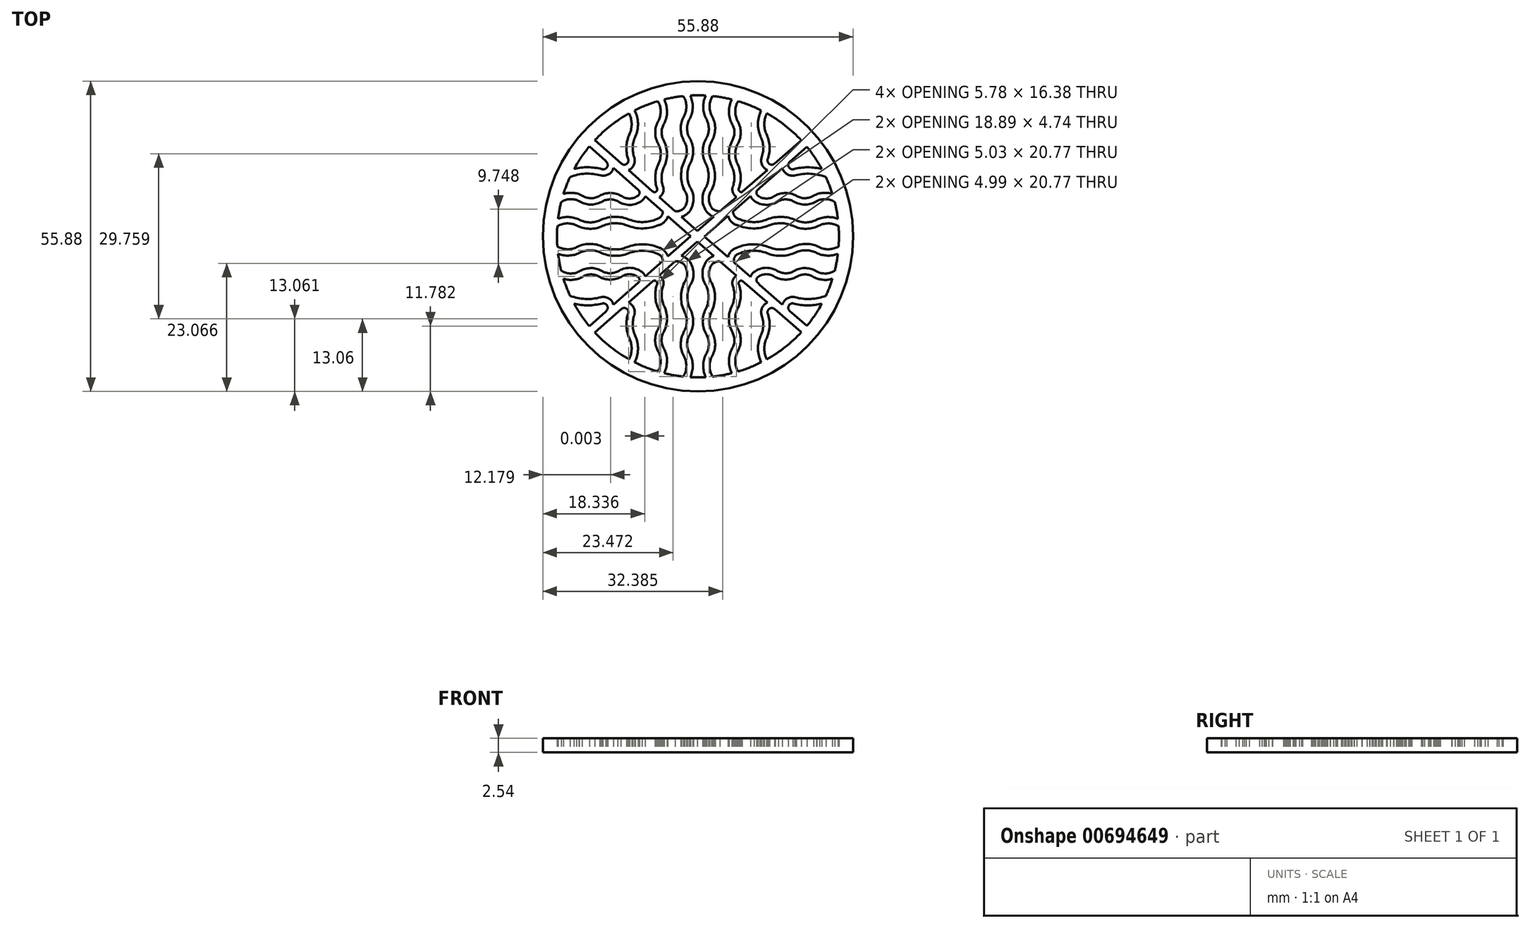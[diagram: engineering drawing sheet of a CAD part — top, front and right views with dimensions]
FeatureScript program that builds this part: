
annotation { "Feature Type Name" : "Feature", "Feature Type Description" : "" }
export const myFeature = defineFeature(function(context is Context, id is Id, definition is map)
    precondition{}
    {
        {
            var Q0;
            Q0=qCreatedBy(makeId("Top.planeOp"),FACE);
            var sketch = newSketch(context, id + "F0", { "sketchPlane" : qUnion([Q0])});
            skArc(sketch, "E0", {"start": v(11.4, 22.7) * mm, "mid": v(9.36, 23.61) * mm, "end": v(7.23, 24.35) * mm});
            skLineSegment(sketch, "E1.0", {"start": v(-19.59, 16.2) * mm, "end": v(-16.64, 13.58) * mm});
            skLineSegment(sketch, "E2.trimOffspring", {"start": v(-15.2, 12.3) * mm, "end": v(-11.27, 8.82) * mm});
            skLineSegment(sketch, "E3.trimOffspring", {"start": v(-9.5, 7.24) * mm, "end": v(-6.32, 4.43) * mm});
            skPoint(sketch, "E4.orphan", {"position": v(-12.42, 13.76) * mm});
            skLineSegment(sketch, "E5.trimOffspring", {"start": v(-12.5, 11.94) * mm, "end": v(-8.15, 8.09) * mm});
            skLineSegment(sketch, "E6.trimOffspring", {"start": v(-5.42, 3.63) * mm, "end": v(-1.33, 0) * mm});
            skPoint(sketch, "E7.endSnap0", {"position": v(-6.51, 7.74) * mm});
            skPoint(sketch, "E8.orphan", {"position": v(-7.23, 8.52) * mm});
            skLineSegment(sketch, "E9.trimOffspring", {"start": v(-6.99, 7.05) * mm, "end": v(-4.1, 4.5) * mm});
            skPoint(sketch, "E10.orphan", {"position": v(-2.63, 4.8) * mm});
            skLineSegment(sketch, "E11.trimOffspring", {"start": v(-2.98, 3.5) * mm, "end": v(-0.1, 0.94) * mm});
            skArc(sketch, "E12.MirrorCS", {"start": v(7.42, 3.1) * mm, "mid": v(6.64, 3.6) * mm, "end": v(6.32, 4.47) * mm});
            skLineSegment(sketch, "E13", {"start": v(19.61, 16.14) * mm, "end": v(16.53, 13.44) * mm});
            skPoint(sketch, "E14.orphan", {"position": v(5.96, 8.48) * mm});
            skLineSegment(sketch, "E15.trimOffspring", {"start": v(15.2, 12.28) * mm, "end": v(11.15, 8.71) * mm});
            skLineSegment(sketch, "E16.trimOffspring", {"start": v(12.5, 11.94) * mm, "end": v(8.02, 8.03) * mm});
            skPoint(sketch, "E17.orphan", {"position": v(12.33, 13.66) * mm});
            skLineSegment(sketch, "E18.trimOffspring", {"start": v(9.49, 7.26) * mm, "end": v(6.32, 4.47) * mm});
            skLineSegment(sketch, "E19.trimOffspring", {"start": v(6.94, 7.08) * mm, "end": v(3.98, 4.5) * mm});
            skLineSegment(sketch, "E20.trimOffspring", {"start": v(5.41, 3.68) * mm, "end": v(1.18, -0.03) * mm});
            skLineSegment(sketch, "E21.trimOffspring", {"start": v(2.87, 3.53) * mm, "end": v(-0.1, 0.94) * mm});
            skPoint(sketch, "E22.orphan", {"position": v(7.1, 8.47) * mm});
            skPoint(sketch, "E23.orphan", {"position": v(2.47, 4.78) * mm});
            skLineSegment(sketch, "E24", {"start": v(-1.33, 0) * mm, "end": v(-5.42, -3.63) * mm});
            skLineSegment(sketch, "E25", {"start": v(-0.1, -0.93) * mm, "end": v(-3, -3.49) * mm});
            skLineSegment(sketch, "E26.trimOffspring", {"start": v(-16.62, -13.56) * mm, "end": v(-19.58, -16.18) * mm});
            skLineSegment(sketch, "E27", {"start": v(-4.1, -4.5) * mm, "end": v(-6.99, -7.05) * mm});
            skLineSegment(sketch, "E28", {"start": v(-8.15, -8.09) * mm, "end": v(-12.5, -11.94) * mm});
            skLineSegment(sketch, "E29", {"start": v(-13.8, -13.1) * mm, "end": v(-18.57, -17.33) * mm});
            skPoint(sketch, "E30.MirrorP", {"position": v(12.33, -13.66) * mm});
            skLineSegment(sketch, "E31", {"start": v(-0.1, -0.93) * mm, "end": v(2.87, -3.53) * mm});
            skLineSegment(sketch, "E32", {"start": v(1.18, -0.03) * mm, "end": v(5.45, -3.76) * mm});
            skLineSegment(sketch, "E33", {"start": v(7.97, -7.99) * mm, "end": v(12.5, -11.94) * mm});
            skLineSegment(sketch, "E34", {"start": v(19.62, -16.13) * mm, "end": v(16.53, -13.44) * mm});
            skLineSegment(sketch, "E35.trimOffspring", {"start": v(3.98, -4.5) * mm, "end": v(6.94, -7.08) * mm});
            skLineSegment(sketch, "E36.trimOffspring", {"start": v(6.55, -4.72) * mm, "end": v(9.48, -7.28) * mm});
            skLineSegment(sketch, "E37.trimOffspring", {"start": v(15.2, -12.28) * mm, "end": v(11.14, -8.73) * mm});
            skPoint(sketch, "E38.orphan", {"position": v(-1.2, -0.1) * mm});
            skCircle(sketch, "E39.0", {"center": v(0, 0) * mm, "radius": 27.94 * mm});
            skArc(sketch, "E40.trimOffspring", {"start": v(6.1, 24.66) * mm, "mid": v(4.37, 25.02) * mm, "end": v(2.63, 25.26) * mm});
            skArc(sketch, "E41.trimOffspring", {"start": v(1.39, 25.36) * mm, "mid": v(0, 25.4) * mm, "end": v(-1.39, 25.36) * mm});
            skArc(sketch, "E42.trimOffspring", {"start": v(-2.63, 25.26) * mm, "mid": v(-4.37, 25.02) * mm, "end": v(-6.1, 24.66) * mm});
            skArc(sketch, "E43.trimOffspring", {"start": v(-7.23, 24.35) * mm, "mid": v(-9.36, 23.61) * mm, "end": v(-11.4, 22.7) * mm});
            skArc(sketch, "E44.trimOffspring", {"start": v(-12.42, 22.16) * mm, "mid": v(-15.68, 19.98) * mm, "end": v(-18.57, 17.33) * mm});
            skArc(sketch, "E45.trimOffspring", {"start": v(-19.58, 16.18) * mm, "mid": v(-21.04, 14.22) * mm, "end": v(-22.32, 12.13) * mm});
            skArc(sketch, "E46.trimOffspring", {"start": v(-23.03, 10.7) * mm, "mid": v(-23.68, 9.2) * mm, "end": v(-24.22, 7.64) * mm});
            skArc(sketch, "E47.trimOffspring", {"start": v(-24.63, 6.2) * mm, "mid": v(-24.96, 4.68) * mm, "end": v(-25.2, 3.15) * mm});
            skArc(sketch, "E48.trimOffspring", {"start": v(-25.33, 1.82) * mm, "mid": v(-25.4, 0) * mm, "end": v(-25.33, -1.82) * mm});
            skArc(sketch, "E49.trimOffspring", {"start": v(-25.2, -3.15) * mm, "mid": v(-24.96, -4.68) * mm, "end": v(-24.63, -6.2) * mm});
            skArc(sketch, "E50.trimOffspring", {"start": v(-22.32, -12.13) * mm, "mid": v(-21.04, -14.22) * mm, "end": v(-19.58, -16.18) * mm});
            skArc(sketch, "E51.trimOffspring", {"start": v(-18.57, -17.33) * mm, "mid": v(-15.68, -19.98) * mm, "end": v(-12.42, -22.16) * mm});
            skArc(sketch, "E52.trimOffspring", {"start": v(-11.4, -22.7) * mm, "mid": v(-9.36, -23.61) * mm, "end": v(-7.23, -24.35) * mm});
            skArc(sketch, "E53.trimOffspring", {"start": v(-6.1, -24.66) * mm, "mid": v(-4.37, -25.02) * mm, "end": v(-2.63, -25.26) * mm});
            skArc(sketch, "E54.trimOffspring", {"start": v(-1.39, -25.36) * mm, "mid": v(0, -25.4) * mm, "end": v(1.39, -25.36) * mm});
            skArc(sketch, "E55.trimOffspring", {"start": v(2.63, -25.26) * mm, "mid": v(4.37, -25.02) * mm, "end": v(6.1, -24.66) * mm});
            skArc(sketch, "E56.trimOffspring", {"start": v(7.23, -24.35) * mm, "mid": v(9.36, -23.61) * mm, "end": v(11.4, -22.7) * mm});
            skArc(sketch, "E57.trimOffspring", {"start": v(12.42, -22.16) * mm, "mid": v(15.7, -19.96) * mm, "end": v(18.62, -17.28) * mm});
            skArc(sketch, "E58.trimOffspring", {"start": v(19.62, -16.13) * mm, "mid": v(21.06, -14.2) * mm, "end": v(22.32, -12.13) * mm});
            skArc(sketch, "E59.trimOffspring", {"start": v(23.03, -10.7) * mm, "mid": v(23.68, -9.2) * mm, "end": v(24.22, -7.64) * mm});
            skArc(sketch, "E60.trimOffspring", {"start": v(24.63, -6.2) * mm, "mid": v(24.96, -4.68) * mm, "end": v(25.2, -3.15) * mm});
            skArc(sketch, "E61.trimOffspring", {"start": v(25.33, -1.82) * mm, "mid": v(25.4, 0) * mm, "end": v(25.33, 1.82) * mm});
            skArc(sketch, "E62.trimOffspring", {"start": v(25.2, 3.15) * mm, "mid": v(24.96, 4.68) * mm, "end": v(24.63, 6.2) * mm});
            skArc(sketch, "E63.trimOffspring", {"start": v(24.22, 7.64) * mm, "mid": v(23.68, 9.18) * mm, "end": v(23.05, 10.68) * mm});
            skArc(sketch, "E64.trimOffspring", {"start": v(22.33, 12.1) * mm, "mid": v(21.07, 14.19) * mm, "end": v(19.61, 16.14) * mm});
            skArc(sketch, "E65.trimOffspring", {"start": v(18.62, 17.28) * mm, "mid": v(15.7, 19.96) * mm, "end": v(12.42, 22.16) * mm});
            skArc(sketch, "E66", {"start": v(23.05, 10.68) * mm, "mid": v(20.32, 11.27) * mm, "end": v(17.54, 10.99) * mm});
            skArc(sketch, "E67.0", {"start": v(22.33, 12.1) * mm, "mid": v(19.79, 12.43) * mm, "end": v(17.25, 12.1) * mm});
            skArc(sketch, "E68", {"start": v(16.53, 13.44) * mm, "mid": v(16.36, 12.48) * mm, "end": v(17.25, 12.1) * mm});
            skArc(sketch, "E69.0", {"start": v(15.2, 12.28) * mm, "mid": v(16.11, 11.16) * mm, "end": v(17.54, 10.99) * mm});
            skArc(sketch, "E70.trimOffspring", {"start": v(15.67, 12.68) * mm, "mid": v(15.67, 12.68) * mm, "end": v(15.67, 12.69) * mm});
            skArc(sketch, "E71.MirrorCS", {"start": v(16.53, -13.44) * mm, "mid": v(16.36, -12.48) * mm, "end": v(17.24, -12.1) * mm});
            skArc(sketch, "E72.MirrorCS", {"start": v(15.2, -12.28) * mm, "mid": v(16.11, -11.17) * mm, "end": v(17.53, -10.99) * mm});
            skArc(sketch, "E73.MirrorCS", {"start": v(22.32, -12.13) * mm, "mid": v(19.78, -12.44) * mm, "end": v(17.24, -12.1) * mm});
            skArc(sketch, "E74.MirrorCS", {"start": v(23.03, -10.7) * mm, "mid": v(20.3, -11.28) * mm, "end": v(17.53, -10.99) * mm});
            skPoint(sketch, "E75.orphan", {"position": v(15.2, -12.28) * mm});
            skPoint(sketch, "E76.endSnap0", {"position": v(0, -25.4) * mm});
            skArc(sketch, "E77.MirrorCS", {"start": v(-16.53, -13.44) * mm, "mid": v(-16.36, -12.48) * mm, "end": v(-17.24, -12.1) * mm});
            skArc(sketch, "E78.MirrorCS", {"start": v(-15.2, -12.3) * mm, "mid": v(-16.1, -11.17) * mm, "end": v(-17.53, -10.99) * mm});
            skArc(sketch, "E79.MirrorCS", {"start": v(-23.03, -10.7) * mm, "mid": v(-20.3, -11.28) * mm, "end": v(-17.53, -10.99) * mm});
            skArc(sketch, "E80.MirrorCS", {"start": v(-22.32, -12.13) * mm, "mid": v(-19.78, -12.44) * mm, "end": v(-17.24, -12.1) * mm});
            skArc(sketch, "E81.MirrorCS", {"start": v(-16.53, 13.44) * mm, "mid": v(-16.36, 12.48) * mm, "end": v(-17.24, 12.1) * mm});
            skArc(sketch, "E82.MirrorCS", {"start": v(-22.32, 12.13) * mm, "mid": v(-19.78, 12.44) * mm, "end": v(-17.24, 12.1) * mm});
            skArc(sketch, "E83.MirrorCS", {"start": v(-23.03, 10.7) * mm, "mid": v(-20.3, 11.28) * mm, "end": v(-17.53, 10.99) * mm});
            skArc(sketch, "E84.MirrorCS", {"start": v(-15.2, 12.3) * mm, "mid": v(-16.1, 11.17) * mm, "end": v(-17.53, 10.99) * mm});
            skPoint(sketch, "E85.orphan", {"position": v(-15.2, 12.28) * mm});
            skLineSegment(sketch, "E86", {"start": v(-16.64, 13.58) * mm, "end": v(-16.53, 13.44) * mm});
            skPoint(sketch, "E87.orphan", {"position": v(-15.2, -12.28) * mm});
            skLineSegment(sketch, "E88", {"start": v(-16.62, -13.56) * mm, "end": v(-16.53, -13.44) * mm});
            skArc(sketch, "E89", {"start": v(-12.42, -22.16) * mm, "mid": v(-11.95, -20.32) * mm, "end": v(-12.31, -18.46) * mm});
            skArc(sketch, "E90.0", {"start": v(-11.4, -22.7) * mm, "mid": v(-10.81, -20.35) * mm, "end": v(-11.27, -17.98) * mm});
            skArc(sketch, "E91", {"start": v(-11.44, -14.13) * mm, "mid": v(-11.76, -16.08) * mm, "end": v(-11.27, -17.98) * mm});
            skArc(sketch, "E92.0", {"start": v(-12.55, -13.83) * mm, "mid": v(-12.9, -16.17) * mm, "end": v(-12.31, -18.46) * mm});
            skArc(sketch, "E93", {"start": v(-12.55, -13.83) * mm, "mid": v(-12.9, -13.01) * mm, "end": v(-13.8, -13.1) * mm});
            skArc(sketch, "E94.0", {"start": v(-11.42, -14.03) * mm, "mid": v(-11.6, -12.8) * mm, "end": v(-12.5, -11.94) * mm});
            skLineSegment(sketch, "E95", {"start": v(-11.42, -14.03) * mm, "end": v(-11.44, -14.13) * mm});
            skArc(sketch, "E96.MirrorCS", {"start": v(12.55, -13.83) * mm, "mid": v(12.9, -13.01) * mm, "end": v(13.8, -13.1) * mm});
            skArc(sketch, "E97.MirrorCS", {"start": v(11.42, -14.03) * mm, "mid": v(11.6, -12.8) * mm, "end": v(12.5, -11.94) * mm});
            skArc(sketch, "E98.MirrorCS", {"start": v(11.44, -14.13) * mm, "mid": v(11.76, -16.08) * mm, "end": v(11.27, -17.98) * mm});
            skArc(sketch, "E99.MirrorCS", {"start": v(12.55, -13.83) * mm, "mid": v(12.9, -16.17) * mm, "end": v(12.31, -18.46) * mm});
            skLineSegment(sketch, "E100.MirrorCS", {"start": v(11.42, -14.03) * mm, "end": v(11.44, -14.13) * mm});
            skArc(sketch, "E101.MirrorCS", {"start": v(12.42, -22.16) * mm, "mid": v(11.95, -20.32) * mm, "end": v(12.31, -18.46) * mm});
            skArc(sketch, "E102.MirrorCS", {"start": v(11.4, -22.7) * mm, "mid": v(10.81, -20.35) * mm, "end": v(11.27, -17.98) * mm});
            skLineSegment(sketch, "E103", {"start": v(18.62, -17.28) * mm, "end": v(13.8, -13.1) * mm});
            skPoint(sketch, "E104.orphan", {"position": v(12.5, -11.94) * mm});
            skArc(sketch, "E105.MirrorCS", {"start": v(12.55, 13.83) * mm, "mid": v(12.9, 16.17) * mm, "end": v(12.31, 18.46) * mm});
            skArc(sketch, "E106.MirrorCS", {"start": v(11.44, 14.13) * mm, "mid": v(11.76, 16.08) * mm, "end": v(11.27, 17.98) * mm});
            skArc(sketch, "E107.MirrorCS", {"start": v(11.4, 22.7) * mm, "mid": v(10.81, 20.35) * mm, "end": v(11.27, 17.98) * mm});
            skArc(sketch, "E108.MirrorCS", {"start": v(12.42, 22.16) * mm, "mid": v(11.95, 20.32) * mm, "end": v(12.31, 18.46) * mm});
            skArc(sketch, "E109.MirrorCS", {"start": v(11.42, 14.03) * mm, "mid": v(11.6, 12.8) * mm, "end": v(12.5, 11.94) * mm});
            skArc(sketch, "E110.MirrorCS", {"start": v(12.55, 13.83) * mm, "mid": v(12.9, 13.01) * mm, "end": v(13.8, 13.1) * mm});
            skLineSegment(sketch, "E111.MirrorCS", {"start": v(11.42, 14.03) * mm, "end": v(11.44, 14.13) * mm});
            skLineSegment(sketch, "E112", {"start": v(13.8, 13.1) * mm, "end": v(18.62, 17.28) * mm});
            skArc(sketch, "E113.MirrorCS", {"start": v(-11.4, 22.7) * mm, "mid": v(-10.81, 20.35) * mm, "end": v(-11.27, 17.98) * mm});
            skArc(sketch, "E114.MirrorCS", {"start": v(-12.42, 22.16) * mm, "mid": v(-11.95, 20.32) * mm, "end": v(-12.31, 18.46) * mm});
            skArc(sketch, "E115.MirrorCS", {"start": v(-12.55, 13.84) * mm, "mid": v(-12.9, 16.17) * mm, "end": v(-12.31, 18.46) * mm});
            skArc(sketch, "E116.MirrorCS", {"start": v(-11.44, 14.13) * mm, "mid": v(-11.76, 16.08) * mm, "end": v(-11.27, 17.98) * mm});
            skLineSegment(sketch, "E117.MirrorCS", {"start": v(-11.42, 14.03) * mm, "end": v(-11.44, 14.13) * mm});
            skArc(sketch, "E118.MirrorCS", {"start": v(-11.42, 14.03) * mm, "mid": v(-11.6, 12.8) * mm, "end": v(-12.5, 11.94) * mm});
            skArc(sketch, "E119.MirrorCS", {"start": v(-12.55, 13.84) * mm, "mid": v(-12.9, 13.01) * mm, "end": v(-13.8, 13.1) * mm});
            skPoint(sketch, "E120.orphan", {"position": v(-12.5, 11.94) * mm});
            skLineSegment(sketch, "E121", {"start": v(-18.57, 17.33) * mm, "end": v(-13.8, 13.1) * mm});
            skArc(sketch, "E122", {"start": v(-24.63, -6.2) * mm, "mid": v(-23.05, -6.7) * mm, "end": v(-21.43, -6.35) * mm});
            skArc(sketch, "E123.0", {"start": v(-24.22, -7.64) * mm, "mid": v(-22.5, -7.83) * mm, "end": v(-20.86, -7.34) * mm});
            skArc(sketch, "E124", {"start": v(-17.73, -7.31) * mm, "mid": v(-19.3, -6.87) * mm, "end": v(-20.86, -7.34) * mm});
            skArc(sketch, "E125.0", {"start": v(-17.39, -6.2) * mm, "mid": v(-19.43, -5.73) * mm, "end": v(-21.43, -6.35) * mm});
            skArc(sketch, "E126", {"start": v(-17.39, -6.2) * mm, "mid": v(-15.96, -6.65) * mm, "end": v(-14.49, -6.36) * mm});
            skArc(sketch, "E127.0", {"start": v(-17.73, -7.31) * mm, "mid": v(-15.81, -7.8) * mm, "end": v(-13.9, -7.34) * mm});
            skArc(sketch, "E128", {"start": v(-10.78, -7.34) * mm, "mid": v(-12.34, -6.82) * mm, "end": v(-13.9, -7.34) * mm});
            skArc(sketch, "E129.0", {"start": v(-10.1, -6.42) * mm, "mid": v(-12.28, -5.67) * mm, "end": v(-14.49, -6.36) * mm});
            skArc(sketch, "E130", {"start": v(-10.78, -8.38) * mm, "mid": v(-10.53, -7.86) * mm, "end": v(-10.78, -7.34) * mm});
            skArc(sketch, "E131.0", {"start": v(-9.5, -7.24) * mm, "mid": v(-9.73, -6.8) * mm, "end": v(-10.08, -6.43) * mm});
            skLineSegment(sketch, "E132.trimOffspring", {"start": v(-10.74, -8.34) * mm, "end": v(-15.2, -12.3) * mm});
            skLineSegment(sketch, "E133", {"start": v(-10.1, -6.42) * mm, "end": v(-10.08, -6.43) * mm});
            skArc(sketch, "E134.MirrorCS", {"start": v(24.22, -7.64) * mm, "mid": v(22.5, -7.83) * mm, "end": v(20.86, -7.34) * mm});
            skArc(sketch, "E135.MirrorCS", {"start": v(24.63, -6.2) * mm, "mid": v(23.05, -6.7) * mm, "end": v(21.43, -6.35) * mm});
            skArc(sketch, "E136.MirrorCS", {"start": v(17.39, -6.2) * mm, "mid": v(19.43, -5.73) * mm, "end": v(21.43, -6.35) * mm});
            skArc(sketch, "E137.MirrorCS", {"start": v(17.73, -7.31) * mm, "mid": v(19.3, -6.87) * mm, "end": v(20.86, -7.34) * mm});
            skArc(sketch, "E138.MirrorCS", {"start": v(17.39, -6.2) * mm, "mid": v(15.96, -6.65) * mm, "end": v(14.49, -6.36) * mm});
            skArc(sketch, "E139.MirrorCS", {"start": v(17.73, -7.31) * mm, "mid": v(15.81, -7.8) * mm, "end": v(13.9, -7.34) * mm});
            skArc(sketch, "E140.MirrorCS", {"start": v(10.1, -6.42) * mm, "mid": v(12.28, -5.67) * mm, "end": v(14.49, -6.36) * mm});
            skArc(sketch, "E141.MirrorCS", {"start": v(10.78, -7.34) * mm, "mid": v(12.34, -6.82) * mm, "end": v(13.9, -7.34) * mm});
            skArc(sketch, "E142.MirrorCS", {"start": v(10.78, -8.38) * mm, "mid": v(10.53, -7.86) * mm, "end": v(10.78, -7.34) * mm});
            skArc(sketch, "E143.MirrorCS", {"start": v(9.48, -7.28) * mm, "mid": v(9.72, -6.81) * mm, "end": v(10.08, -6.43) * mm});
            skLineSegment(sketch, "E144.MirrorCS", {"start": v(10.1, -6.42) * mm, "end": v(10.08, -6.43) * mm});
            skPoint(sketch, "E145.orphan", {"position": v(9.5, -7.24) * mm});
            skLineSegment(sketch, "E146", {"start": v(11.14, -8.73) * mm, "end": v(10.78, -8.38) * mm});
            skArc(sketch, "E147.MirrorCS", {"start": v(10.1, 6.42) * mm, "mid": v(12.28, 5.67) * mm, "end": v(14.49, 6.36) * mm});
            skArc(sketch, "E148.MirrorCS", {"start": v(9.49, 7.26) * mm, "mid": v(9.72, 6.8) * mm, "end": v(10.08, 6.43) * mm});
            skArc(sketch, "E149.MirrorCS", {"start": v(10.78, 7.34) * mm, "mid": v(12.34, 6.82) * mm, "end": v(13.9, 7.34) * mm});
            skArc(sketch, "E150.MirrorCS", {"start": v(10.78, 8.38) * mm, "mid": v(10.53, 7.86) * mm, "end": v(10.78, 7.34) * mm});
            skArc(sketch, "E151.MirrorCS", {"start": v(17.73, 7.31) * mm, "mid": v(15.81, 7.8) * mm, "end": v(13.9, 7.34) * mm});
            skArc(sketch, "E152.MirrorCS", {"start": v(17.39, 6.2) * mm, "mid": v(15.96, 6.65) * mm, "end": v(14.49, 6.36) * mm});
            skArc(sketch, "E153.MirrorCS", {"start": v(17.73, 7.31) * mm, "mid": v(19.3, 6.87) * mm, "end": v(20.86, 7.34) * mm});
            skArc(sketch, "E154.MirrorCS", {"start": v(17.39, 6.2) * mm, "mid": v(19.43, 5.73) * mm, "end": v(21.43, 6.35) * mm});
            skArc(sketch, "E155.MirrorCS", {"start": v(24.22, 7.64) * mm, "mid": v(22.5, 7.83) * mm, "end": v(20.86, 7.34) * mm});
            skArc(sketch, "E156.MirrorCS", {"start": v(24.63, 6.2) * mm, "mid": v(23.05, 6.7) * mm, "end": v(21.43, 6.35) * mm});
            skLineSegment(sketch, "E157", {"start": v(11.15, 8.71) * mm, "end": v(10.78, 8.38) * mm});
            skPoint(sketch, "E158.orphan", {"position": v(9.48, 7.28) * mm});
            skLineSegment(sketch, "E159", {"start": v(10.08, 6.43) * mm, "end": v(10.1, 6.42) * mm});
            skArc(sketch, "E160.MirrorCS", {"start": v(-10.78, 8.38) * mm, "mid": v(-10.53, 7.86) * mm, "end": v(-10.78, 7.34) * mm});
            skArc(sketch, "E161.MirrorCS", {"start": v(-9.5, 7.24) * mm, "mid": v(-9.74, 6.78) * mm, "end": v(-10.11, 6.4) * mm});
            skArc(sketch, "E162.MirrorCS", {"start": v(-10.11, 6.4) * mm, "mid": v(-12.3, 5.67) * mm, "end": v(-14.49, 6.36) * mm});
            skArc(sketch, "E163.MirrorCS", {"start": v(-10.78, 7.34) * mm, "mid": v(-12.34, 6.82) * mm, "end": v(-13.9, 7.34) * mm});
            skArc(sketch, "E164.MirrorCS", {"start": v(-17.38, 6.2) * mm, "mid": v(-15.95, 6.65) * mm, "end": v(-14.49, 6.36) * mm});
            skArc(sketch, "E165.MirrorCS", {"start": v(-17.73, 7.31) * mm, "mid": v(-15.81, 7.8) * mm, "end": v(-13.9, 7.34) * mm});
            skArc(sketch, "E166.MirrorCS", {"start": v(-17.17, 6.32) * mm, "mid": v(-19.3, 5.72) * mm, "end": v(-21.43, 6.35) * mm});
            skArc(sketch, "E167.MirrorCS", {"start": v(-17.73, 7.31) * mm, "mid": v(-19.3, 6.87) * mm, "end": v(-20.86, 7.34) * mm});
            skArc(sketch, "E168.MirrorCS", {"start": v(-24.63, 6.2) * mm, "mid": v(-23.05, 6.7) * mm, "end": v(-21.43, 6.35) * mm});
            skArc(sketch, "E169.MirrorCS", {"start": v(-24.22, 7.64) * mm, "mid": v(-22.5, 7.83) * mm, "end": v(-20.86, 7.34) * mm});
            skLineSegment(sketch, "E170", {"start": v(-11.27, 8.82) * mm, "end": v(-10.78, 8.38) * mm});
            skPoint(sketch, "E171.orphan", {"position": v(-10.4, 8.04) * mm});
            skArc(sketch, "E172", {"start": v(-7.09, 20.86) * mm, "mid": v(-6.72, 22.62) * mm, "end": v(-7.23, 24.35) * mm});
            skArc(sketch, "E173.0", {"start": v(-6.09, 20.3) * mm, "mid": v(-5.57, 22.48) * mm, "end": v(-6.1, 24.66) * mm});
            skArc(sketch, "E174", {"start": v(-6.09, 20.3) * mm, "mid": v(-6.56, 18.84) * mm, "end": v(-6.22, 17.34) * mm});
            skArc(sketch, "E175.0", {"start": v(-7.09, 20.86) * mm, "mid": v(-7.7, 18.85) * mm, "end": v(-7.22, 16.8) * mm});
            skArc(sketch, "E176", {"start": v(-7.12, 13.06) * mm, "mid": v(-6.7, 14.94) * mm, "end": v(-7.22, 16.8) * mm});
            skArc(sketch, "E177.0", {"start": v(-6.1, 12.56) * mm, "mid": v(-5.57, 14.97) * mm, "end": v(-6.22, 17.34) * mm});
            skArc(sketch, "E178", {"start": v(-6.1, 12.56) * mm, "mid": v(-6.56, 10.74) * mm, "end": v(-6.25, 8.88) * mm});
            skArc(sketch, "E179.0", {"start": v(-7.12, 13.06) * mm, "mid": v(-7.7, 10.83) * mm, "end": v(-7.34, 8.54) * mm});
            skArc(sketch, "E180", {"start": v(-8.15, 8.09) * mm, "mid": v(-7.58, 8.03) * mm, "end": v(-7.34, 8.54) * mm});
            skArc(sketch, "E181.0", {"start": v(-6.99, 7.05) * mm, "mid": v(-6.31, 7.84) * mm, "end": v(-6.25, 8.88) * mm});
            skArc(sketch, "E182.MirrorCS", {"start": v(-6.99, -7.05) * mm, "mid": v(-6.31, -7.84) * mm, "end": v(-6.25, -8.88) * mm});
            skArc(sketch, "E183.MirrorCS", {"start": v(-8.15, -8.09) * mm, "mid": v(-7.58, -8.03) * mm, "end": v(-7.34, -8.54) * mm});
            skArc(sketch, "E184.MirrorCS", {"start": v(-7.12, -13.07) * mm, "mid": v(-7.7, -10.83) * mm, "end": v(-7.34, -8.54) * mm});
            skArc(sketch, "E185.MirrorCS", {"start": v(-6.09, -12.56) * mm, "mid": v(-6.56, -10.74) * mm, "end": v(-6.25, -8.88) * mm});
            skArc(sketch, "E186.MirrorCS", {"start": v(-7.12, -13.07) * mm, "mid": v(-6.72, -14.94) * mm, "end": v(-7.23, -16.8) * mm});
            skArc(sketch, "E187.MirrorCS", {"start": v(-6.09, -12.56) * mm, "mid": v(-5.57, -14.97) * mm, "end": v(-6.23, -17.34) * mm});
            skArc(sketch, "E188.MirrorCS", {"start": v(-7.09, -20.86) * mm, "mid": v(-7.7, -18.85) * mm, "end": v(-7.23, -16.8) * mm});
            skArc(sketch, "E189.MirrorCS", {"start": v(-6.09, -20.3) * mm, "mid": v(-6.56, -18.84) * mm, "end": v(-6.23, -17.34) * mm});
            skArc(sketch, "E190.MirrorCS", {"start": v(-7.09, -20.86) * mm, "mid": v(-6.72, -22.62) * mm, "end": v(-7.23, -24.35) * mm});
            skArc(sketch, "E191.MirrorCS", {"start": v(-6.09, -20.3) * mm, "mid": v(-5.57, -22.48) * mm, "end": v(-6.1, -24.66) * mm});
            skArc(sketch, "E192.MirrorCS", {"start": v(-6.09, -20.3) * mm, "mid": v(-5.57, -22.47) * mm, "end": v(-6.09, -24.64) * mm});
            skPoint(sketch, "E193.orphan", {"position": v(-6.09, -24.64) * mm});
            skArc(sketch, "E194.MirrorCS", {"start": v(6.94, -7.08) * mm, "mid": v(6.26, -8) * mm, "end": v(6.34, -9.13) * mm});
            skArc(sketch, "E195.MirrorCS", {"start": v(7.97, -7.99) * mm, "mid": v(7.5, -8.09) * mm, "end": v(7.34, -8.54) * mm});
            skArc(sketch, "E196.MirrorCS", {"start": v(7.12, -13.07) * mm, "mid": v(7.7, -10.83) * mm, "end": v(7.34, -8.54) * mm});
            skArc(sketch, "E197.MirrorCS", {"start": v(6.09, -12.57) * mm, "mid": v(6.55, -10.87) * mm, "end": v(6.34, -9.13) * mm});
            skArc(sketch, "E198.MirrorCS", {"start": v(7.12, -13.07) * mm, "mid": v(6.72, -14.94) * mm, "end": v(7.23, -16.8) * mm});
            skArc(sketch, "E199.MirrorCS", {"start": v(6.09, -12.57) * mm, "mid": v(5.57, -14.97) * mm, "end": v(6.23, -17.34) * mm});
            skArc(sketch, "E200.MirrorCS", {"start": v(7.09, -20.86) * mm, "mid": v(7.7, -18.85) * mm, "end": v(7.23, -16.8) * mm});
            skArc(sketch, "E201.MirrorCS", {"start": v(6.09, -20.3) * mm, "mid": v(6.56, -18.84) * mm, "end": v(6.23, -17.34) * mm});
            skArc(sketch, "E202.MirrorCS", {"start": v(6.09, -20.3) * mm, "mid": v(5.57, -22.48) * mm, "end": v(6.1, -24.66) * mm});
            skArc(sketch, "E203.MirrorCS", {"start": v(7.09, -20.86) * mm, "mid": v(6.72, -22.62) * mm, "end": v(7.23, -24.35) * mm});
            skPoint(sketch, "E204.orphan", {"position": v(6.99, -7.05) * mm});
            skPoint(sketch, "E205.orphan", {"position": v(8.15, -8.09) * mm});
            skArc(sketch, "E206.MirrorCS", {"start": v(7.97, 7.99) * mm, "mid": v(7.5, 8.09) * mm, "end": v(7.34, 8.54) * mm});
            skArc(sketch, "E207.MirrorCS", {"start": v(6.94, 7.08) * mm, "mid": v(6.3, 7.87) * mm, "end": v(6.25, 8.88) * mm});
            skArc(sketch, "E208.MirrorCS", {"start": v(7.12, 13.07) * mm, "mid": v(7.7, 10.83) * mm, "end": v(7.34, 8.54) * mm});
            skArc(sketch, "E209.MirrorCS", {"start": v(6.09, 12.57) * mm, "mid": v(6.56, 10.74) * mm, "end": v(6.25, 8.88) * mm});
            skArc(sketch, "E210.MirrorCS", {"start": v(7.12, 13.07) * mm, "mid": v(6.72, 14.94) * mm, "end": v(7.23, 16.8) * mm});
            skArc(sketch, "E211.MirrorCS", {"start": v(6.09, 12.57) * mm, "mid": v(5.57, 14.97) * mm, "end": v(6.23, 17.34) * mm});
            skArc(sketch, "E212.MirrorCS", {"start": v(6.09, 20.3) * mm, "mid": v(6.56, 18.84) * mm, "end": v(6.23, 17.34) * mm});
            skArc(sketch, "E213.MirrorCS", {"start": v(7.09, 20.86) * mm, "mid": v(7.7, 18.85) * mm, "end": v(7.23, 16.8) * mm});
            skArc(sketch, "E214.MirrorCS", {"start": v(6.09, 20.3) * mm, "mid": v(5.57, 22.48) * mm, "end": v(6.1, 24.66) * mm});
            skArc(sketch, "E215.MirrorCS", {"start": v(7.09, 20.86) * mm, "mid": v(6.72, 22.62) * mm, "end": v(7.23, 24.35) * mm});
            skLineSegment(sketch, "E216", {"start": v(8.02, 8.03) * mm, "end": v(7.97, 7.99) * mm});
            skArc(sketch, "E217.0", {"start": v(21.38, -3) * mm, "mid": v(23.27, -3.47) * mm, "end": v(25.2, -3.15) * mm});
            skArc(sketch, "E218", {"start": v(21.38, -3) * mm, "mid": v(19.5, -2.5) * mm, "end": v(17.6, -2.92) * mm});
            skArc(sketch, "E219.0", {"start": v(21.9, -1.97) * mm, "mid": v(19.52, -1.36) * mm, "end": v(17.12, -1.88) * mm});
            skArc(sketch, "E220.trimOffspring", {"start": v(21.9, -1.97) * mm, "mid": v(23.63, -2.33) * mm, "end": v(25.33, -1.82) * mm});
            skArc(sketch, "E221", {"start": v(12.8, -1.96) * mm, "mid": v(14.96, -2.37) * mm, "end": v(17.12, -1.88) * mm});
            skArc(sketch, "E222.0", {"start": v(12.48, -3.06) * mm, "mid": v(15.06, -3.51) * mm, "end": v(17.6, -2.92) * mm});
            skArc(sketch, "E223", {"start": v(12.48, -3.06) * mm, "mid": v(9.95, -2.57) * mm, "end": v(7.42, -3.1) * mm});
            skArc(sketch, "E224.trimOffspring", {"start": v(12.8, -1.96) * mm, "mid": v(9.92, -1.42) * mm, "end": v(7.05, -2.02) * mm});
            skArc(sketch, "E225", {"start": v(7.42, -3.1) * mm, "mid": v(6.62, -3.71) * mm, "end": v(6.55, -4.72) * mm});
            skArc(sketch, "E226.0", {"start": v(7.05, -2.02) * mm, "mid": v(6, -2.65) * mm, "end": v(5.4, -3.72) * mm});
            skPoint(sketch, "E227.orphan", {"position": v(7.42, -5.48) * mm});
            skArc(sketch, "E228.MirrorCS", {"start": v(7.05, 2.02) * mm, "mid": v(6.01, 2.63) * mm, "end": v(5.41, 3.68) * mm});
            skArc(sketch, "E229.MirrorCS", {"start": v(12.8, 1.96) * mm, "mid": v(9.92, 1.42) * mm, "end": v(7.05, 2.02) * mm});
            skArc(sketch, "E230.MirrorCS", {"start": v(12.48, 3.06) * mm, "mid": v(9.95, 2.57) * mm, "end": v(7.42, 3.1) * mm});
            skArc(sketch, "E231.MirrorCS", {"start": v(12.48, 3.06) * mm, "mid": v(15.06, 3.51) * mm, "end": v(17.6, 2.92) * mm});
            skArc(sketch, "E232.MirrorCS", {"start": v(12.8, 1.96) * mm, "mid": v(14.96, 2.37) * mm, "end": v(17.12, 1.88) * mm});
            skArc(sketch, "E233.MirrorCS", {"start": v(21.9, 1.97) * mm, "mid": v(19.52, 1.36) * mm, "end": v(17.12, 1.88) * mm});
            skArc(sketch, "E234.MirrorCS", {"start": v(21.38, 3) * mm, "mid": v(19.5, 2.5) * mm, "end": v(17.6, 2.92) * mm});
            skArc(sketch, "E235.MirrorCS", {"start": v(21.38, 3) * mm, "mid": v(23.27, 3.47) * mm, "end": v(25.2, 3.15) * mm});
            skArc(sketch, "E236.MirrorCS", {"start": v(21.9, 1.97) * mm, "mid": v(23.63, 2.33) * mm, "end": v(25.33, 1.82) * mm});
            skPoint(sketch, "E237.orphan", {"position": v(5.4, 3.72) * mm});
            skArc(sketch, "E238.MirrorCS", {"start": v(-12.8, 1.96) * mm, "mid": v(-9.92, 1.42) * mm, "end": v(-7.05, 2.02) * mm});
            skArc(sketch, "E239.MirrorCS", {"start": v(-12.36, 3.02) * mm, "mid": v(-9.88, 2.57) * mm, "end": v(-7.42, 3.1) * mm});
            skArc(sketch, "E240.MirrorCS", {"start": v(-7.42, 3.1) * mm, "mid": v(-6.65, 3.58) * mm, "end": v(-6.32, 4.43) * mm});
            skArc(sketch, "E241.MirrorCS", {"start": v(-7.05, 2.02) * mm, "mid": v(-6.03, 2.61) * mm, "end": v(-5.42, 3.63) * mm});
            skArc(sketch, "E242.MirrorCS", {"start": v(-12.8, 1.96) * mm, "mid": v(-14.96, 2.37) * mm, "end": v(-17.12, 1.88) * mm});
            skArc(sketch, "E243.MirrorCS", {"start": v(-12.36, 3.02) * mm, "mid": v(-15, 3.52) * mm, "end": v(-17.6, 2.92) * mm});
            skArc(sketch, "E244.MirrorCS", {"start": v(-21.9, 1.97) * mm, "mid": v(-19.52, 1.36) * mm, "end": v(-17.12, 1.88) * mm});
            skArc(sketch, "E245.MirrorCS", {"start": v(-21.38, 3) * mm, "mid": v(-19.5, 2.5) * mm, "end": v(-17.6, 2.92) * mm});
            skArc(sketch, "E246.MirrorCS", {"start": v(-21.9, 1.97) * mm, "mid": v(-23.63, 2.33) * mm, "end": v(-25.33, 1.82) * mm});
            skArc(sketch, "E247.MirrorCS", {"start": v(-21.38, 3) * mm, "mid": v(-23.27, 3.47) * mm, "end": v(-25.2, 3.15) * mm});
            skPoint(sketch, "E248.orphan", {"position": v(-6.32, 4.47) * mm});
            skPoint(sketch, "E249.orphan", {"position": v(-5.41, 3.68) * mm});
            skArc(sketch, "E250.MirrorCS", {"start": v(-7.05, -2.02) * mm, "mid": v(-6.03, -2.61) * mm, "end": v(-5.42, -3.63) * mm});
            skArc(sketch, "E251.MirrorCS", {"start": v(-7.42, -3.1) * mm, "mid": v(-6.65, -3.58) * mm, "end": v(-6.32, -4.43) * mm});
            skArc(sketch, "E252.MirrorCS", {"start": v(-12.48, -3.06) * mm, "mid": v(-9.95, -2.57) * mm, "end": v(-7.42, -3.1) * mm});
            skArc(sketch, "E253.MirrorCS", {"start": v(-12.8, -1.96) * mm, "mid": v(-9.92, -1.42) * mm, "end": v(-7.05, -2.02) * mm});
            skArc(sketch, "E254.MirrorCS", {"start": v(-12.8, -1.96) * mm, "mid": v(-14.96, -2.37) * mm, "end": v(-17.12, -1.88) * mm});
            skArc(sketch, "E255.MirrorCS", {"start": v(-12.48, -3.06) * mm, "mid": v(-15.06, -3.51) * mm, "end": v(-17.6, -2.92) * mm});
            skArc(sketch, "E256.MirrorCS", {"start": v(-21.9, -1.97) * mm, "mid": v(-19.52, -1.36) * mm, "end": v(-17.12, -1.88) * mm});
            skArc(sketch, "E257.MirrorCS", {"start": v(-21.38, -3) * mm, "mid": v(-19.5, -2.5) * mm, "end": v(-17.6, -2.92) * mm});
            skArc(sketch, "E258.MirrorCS", {"start": v(-21.9, -1.97) * mm, "mid": v(-23.63, -2.33) * mm, "end": v(-25.33, -1.82) * mm});
            skArc(sketch, "E259.MirrorCS", {"start": v(-21.38, -3) * mm, "mid": v(-23.27, -3.47) * mm, "end": v(-25.2, -3.15) * mm});
            skLineSegment(sketch, "E260.trimOffspring", {"start": v(-6.32, -4.43) * mm, "end": v(-9.5, -7.24) * mm});
            skArc(sketch, "E261", {"start": v(2.63, 25.26) * mm, "mid": v(2.09, 23.39) * mm, "end": v(2.6, 21.5) * mm});
            skArc(sketch, "E262.0", {"start": v(1.39, 25.36) * mm, "mid": v(0.95, 23.28) * mm, "end": v(1.45, 21.21) * mm});
            skArc(sketch, "E263", {"start": v(1.49, 17.66) * mm, "mid": v(1.96, 19.44) * mm, "end": v(1.45, 21.21) * mm});
            skArc(sketch, "E264.0", {"start": v(2.57, 17.25) * mm, "mid": v(3.1, 19.36) * mm, "end": v(2.6, 21.48) * mm});
            skArc(sketch, "E265", {"start": v(2.57, 17.25) * mm, "mid": v(2.01, 15.48) * mm, "end": v(2.41, 13.66) * mm});
            skArc(sketch, "E266.0", {"start": v(1.45, 17.6) * mm, "mid": v(0.87, 15.4) * mm, "end": v(1.37, 13.2) * mm});
            skArc(sketch, "E267", {"start": v(1.5, 8.98) * mm, "mid": v(1.9, 11.1) * mm, "end": v(1.37, 13.2) * mm});
            skArc(sketch, "E268.0", {"start": v(2.5, 8.4) * mm, "mid": v(3.05, 11.05) * mm, "end": v(2.41, 13.66) * mm});
            skArc(sketch, "E269", {"start": v(2.5, 8.4) * mm, "mid": v(1.95, 6.77) * mm, "end": v(2.47, 5.12) * mm});
            skArc(sketch, "E270.0", {"start": v(1.5, 8.98) * mm, "mid": v(0.8, 6.67) * mm, "end": v(1.59, 4.4) * mm});
            skArc(sketch, "E271", {"start": v(2.47, 5.12) * mm, "mid": v(3.16, 4.65) * mm, "end": v(3.98, 4.5) * mm});
            skArc(sketch, "E272.0", {"start": v(1.59, 4.4) * mm, "mid": v(2.18, 3.88) * mm, "end": v(2.87, 3.53) * mm});
            skArc(sketch, "E273.MirrorCS", {"start": v(-1.39, 25.36) * mm, "mid": v(-0.95, 23.28) * mm, "end": v(-1.45, 21.21) * mm});
            skArc(sketch, "E274.MirrorCS", {"start": v(-2.63, 25.26) * mm, "mid": v(-2.09, 23.38) * mm, "end": v(-2.6, 21.48) * mm});
            skArc(sketch, "E275.MirrorCS", {"start": v(-2.57, 17.25) * mm, "mid": v(-3.1, 19.36) * mm, "end": v(-2.6, 21.48) * mm});
            skArc(sketch, "E276.MirrorCS", {"start": v(-1.41, 17.54) * mm, "mid": v(-1.96, 19.37) * mm, "end": v(-1.45, 21.21) * mm});
            skArc(sketch, "E277.MirrorCS", {"start": v(-1.41, 17.54) * mm, "mid": v(-0.87, 15.35) * mm, "end": v(-1.4, 13.15) * mm});
            skArc(sketch, "E278.MirrorCS", {"start": v(-2.57, 17.25) * mm, "mid": v(-2.01, 15.48) * mm, "end": v(-2.41, 13.66) * mm});
            skArc(sketch, "E279.MirrorCS", {"start": v(-2.5, 8.4) * mm, "mid": v(-3.05, 11.05) * mm, "end": v(-2.41, 13.66) * mm});
            skArc(sketch, "E280.MirrorCS", {"start": v(-1.5, 8.98) * mm, "mid": v(-1.91, 11.07) * mm, "end": v(-1.4, 13.15) * mm});
            skArc(sketch, "E281.MirrorCS", {"start": v(-2.5, 8.4) * mm, "mid": v(-1.95, 6.77) * mm, "end": v(-2.47, 5.12) * mm});
            skArc(sketch, "E282.MirrorCS", {"start": v(-1.5, 8.98) * mm, "mid": v(-0.8, 6.67) * mm, "end": v(-1.59, 4.4) * mm});
            skArc(sketch, "E283.MirrorCS", {"start": v(-1.59, 4.4) * mm, "mid": v(-2.22, 3.85) * mm, "end": v(-2.98, 3.5) * mm});
            skArc(sketch, "E284.MirrorCS", {"start": v(-2.47, 5.12) * mm, "mid": v(-3.22, 4.62) * mm, "end": v(-4.1, 4.5) * mm});
            skPoint(sketch, "E285.orphan", {"position": v(-3.98, 4.5) * mm});
            skPoint(sketch, "E286.orphan", {"position": v(-2.87, 3.53) * mm});
            skArc(sketch, "E287.MirrorCS", {"start": v(-2.47, -5.12) * mm, "mid": v(-3.22, -4.62) * mm, "end": v(-4.1, -4.5) * mm});
            skArc(sketch, "E288.MirrorCS", {"start": v(-1.59, -4.4) * mm, "mid": v(-2.23, -3.85) * mm, "end": v(-3, -3.49) * mm});
            skArc(sketch, "E289.MirrorCS", {"start": v(-2.57, -17.25) * mm, "mid": v(-2.01, -15.48) * mm, "end": v(-2.41, -13.66) * mm});
            skArc(sketch, "E290.MirrorCS", {"start": v(-2.5, -8.4) * mm, "mid": v(-1.95, -6.77) * mm, "end": v(-2.47, -5.12) * mm});
            skArc(sketch, "E291.MirrorCS", {"start": v(-1.5, -8.98) * mm, "mid": v(-0.8, -6.67) * mm, "end": v(-1.59, -4.4) * mm});
            skArc(sketch, "E292.MirrorCS", {"start": v(-1.5, -8.98) * mm, "mid": v(-1.91, -11.07) * mm, "end": v(-1.4, -13.15) * mm});
            skArc(sketch, "E293.MirrorCS", {"start": v(-2.5, -8.4) * mm, "mid": v(-3.05, -11.05) * mm, "end": v(-2.41, -13.66) * mm});
            skArc(sketch, "E294.MirrorCS", {"start": v(-1.45, -17.6) * mm, "mid": v(-0.87, -15.38) * mm, "end": v(-1.4, -13.15) * mm});
            skArc(sketch, "E295.MirrorCS", {"start": v(-2.57, -17.25) * mm, "mid": v(-3.1, -19.37) * mm, "end": v(-2.6, -21.5) * mm});
            skArc(sketch, "E296.MirrorCS", {"start": v(-1.41, -17.54) * mm, "mid": v(-1.96, -19.37) * mm, "end": v(-1.45, -21.21) * mm});
            skArc(sketch, "E297.MirrorCS", {"start": v(-1.39, -25.36) * mm, "mid": v(-0.95, -23.28) * mm, "end": v(-1.45, -21.21) * mm});
            skArc(sketch, "E298.MirrorCS", {"start": v(-2.63, -25.26) * mm, "mid": v(-2.09, -23.38) * mm, "end": v(-2.6, -21.48) * mm});
            skArc(sketch, "E299.MirrorCS", {"start": v(2.47, -5.12) * mm, "mid": v(3.16, -4.65) * mm, "end": v(3.98, -4.5) * mm});
            skArc(sketch, "E300.MirrorCS", {"start": v(1.59, -4.4) * mm, "mid": v(2.18, -3.88) * mm, "end": v(2.87, -3.53) * mm});
            skArc(sketch, "E301.MirrorCS", {"start": v(1.5, -8.98) * mm, "mid": v(0.8, -6.67) * mm, "end": v(1.59, -4.4) * mm});
            skArc(sketch, "E302.MirrorCS", {"start": v(2.5, -8.4) * mm, "mid": v(1.95, -6.77) * mm, "end": v(2.47, -5.12) * mm});
            skArc(sketch, "E303.MirrorCS", {"start": v(2.5, -8.4) * mm, "mid": v(3.05, -11.05) * mm, "end": v(2.41, -13.66) * mm});
            skArc(sketch, "E304.MirrorCS", {"start": v(1.5, -8.98) * mm, "mid": v(1.9, -11.1) * mm, "end": v(1.37, -13.2) * mm});
            skArc(sketch, "E305.MirrorCS", {"start": v(1.45, -17.6) * mm, "mid": v(0.87, -15.38) * mm, "end": v(1.4, -13.15) * mm});
            skArc(sketch, "E306.MirrorCS", {"start": v(2.57, -17.25) * mm, "mid": v(2.01, -15.48) * mm, "end": v(2.41, -13.66) * mm});
            skArc(sketch, "E307.MirrorCS", {"start": v(1.45, -17.6) * mm, "mid": v(1.96, -19.4) * mm, "end": v(1.45, -21.21) * mm});
            skArc(sketch, "E308.MirrorCS", {"start": v(2.57, -17.25) * mm, "mid": v(3.1, -19.36) * mm, "end": v(2.6, -21.48) * mm});
            skArc(sketch, "E309.MirrorCS", {"start": v(1.39, -25.36) * mm, "mid": v(0.95, -23.28) * mm, "end": v(1.45, -21.21) * mm});
            skArc(sketch, "E310.MirrorCS", {"start": v(2.63, -25.26) * mm, "mid": v(2.09, -23.38) * mm, "end": v(2.6, -21.48) * mm});
            skPoint(sketch, "E311.orphan", {"position": v(2.98, -3.5) * mm});
            skPoint(sketch, "E312.orphan", {"position": v(4.1, -4.5) * mm});
            skPoint(sketch, "E313.orphan", {"position": v(-1.45, 17.6) * mm});
            skPoint(sketch, "E314.orphan", {"position": v(-6.09, 24.64) * mm});
            skPoint(sketch, "E315.orphan", {"position": v(-2.6, 21.5) * mm});
            skPoint(sketch, "E316.orphan", {"position": v(-1.5, 8.98) * mm});
            skPoint(sketch, "E317.orphan", {"position": v(1.4, 13.15) * mm});
            skPoint(sketch, "E318.orphan", {"position": v(1.45, 17.6) * mm});
            skLineSegment(sketch, "E319", {"start": v(1.45, 17.6) * mm, "end": v(1.49, 17.66) * mm});
            skPoint(sketch, "E320.orphan", {"position": v(2.6, 21.5) * mm});
            skLineSegment(sketch, "E321", {"start": v(2.6, 21.5) * mm, "end": v(2.6, 21.48) * mm});
            skLineSegment(sketch, "E322", {"start": v(1.45, -17.6) * mm, "end": v(1.45, -17.6) * mm});
            skArc(sketch, "E323.trimOffspring", {"start": v(-24.22, -7.64) * mm, "mid": v(-23.68, -9.2) * mm, "end": v(-23.03, -10.7) * mm});
            skPoint(sketch, "E324.startSnap0", {"position": v(-21.04, 14.22) * mm});
            skArc(sketch, "E325.extension", {"start": v(2.63, -25.26) * mm, "mid": v(2.63, -25.26) * mm, "end": v(2.63, -25.26) * mm});
            skSolve(sketch);
        }
        {
            var Q0;
            Q0=makeQuery(id+"F0.imprint","IMPRINT",FACE,{"disambiguationData":[TD([[makeQuery(id+"F0.imprint","IMPRINT",EDGE,{"derivedFrom":sQuery(id+"F0.wireOp",EDGE,"E0")}),-1.0]])]});
            extrude(context, id + "F1", {"entities" : qUnion([Q0]), "depth" : 2.54 * mm, "offsetDistance" : 25.4 * mm});
        }
    });
